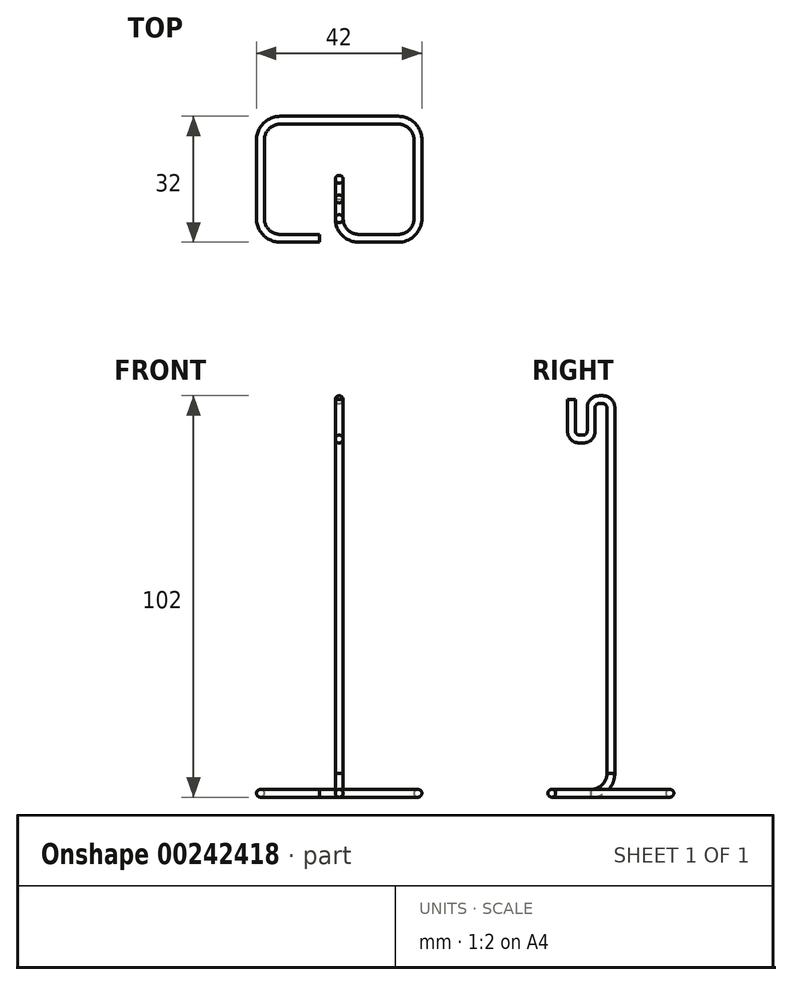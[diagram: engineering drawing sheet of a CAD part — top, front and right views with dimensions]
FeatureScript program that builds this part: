
annotation { "Feature Type Name" : "Feature", "Feature Type Description" : "" }
export const myFeature = defineFeature(function(context is Context, id is Id, definition is map)
    precondition{}
    {
        {
            var Q0;
            Q0=qCreatedBy(makeId("Top.planeOp"),FACE);
            var sketch = newSketch(context, id + "F0", { "sketchPlane" : qUnion([Q0])});
            skLineSegment(sketch, "E0.bottom", {"start": v(-15, 15) * mm, "end": v(15, 15) * mm});
            skLineSegment(sketch, "E0.top", {"start": v(-15, -15) * mm, "end": v(-5, -15) * mm});
            skLineSegment(sketch, "E0.left", {"start": v(-20, 10) * mm, "end": v(-20, -10) * mm});
            skLineSegment(sketch, "E0.right", {"start": v(20, 10) * mm, "end": v(20, -10) * mm});
            skLineSegment(sketch, "E1", {"start": v(0, 0) * mm, "end": v(0, -10) * mm});
            skLineSegment(sketch, "E2.trimOffspring", {"start": v(5, -15) * mm, "end": v(15, -15) * mm});
            skPoint(sketch, "E3.visualSharp", {"position": v(-20, -15) * mm});
            skArc(sketch, "E3.filletArc", {"start": v(-20, -10) * mm, "mid": v(-18.54, -13.54) * mm, "end": v(-15, -15) * mm});
            skPoint(sketch, "E4.visualSharp", {"position": v(-20, 15) * mm});
            skArc(sketch, "E4.filletArc", {"start": v(-15, 15) * mm, "mid": v(-18.54, 13.54) * mm, "end": v(-20, 10) * mm});
            skPoint(sketch, "E5.visualSharp", {"position": v(20, 15) * mm});
            skArc(sketch, "E5.filletArc", {"start": v(20, 10) * mm, "mid": v(18.54, 13.54) * mm, "end": v(15, 15) * mm});
            skPoint(sketch, "E6.visualSharp", {"position": v(20, -15) * mm});
            skArc(sketch, "E6.filletArc", {"start": v(15, -15) * mm, "mid": v(18.54, -13.54) * mm, "end": v(20, -10) * mm});
            skPoint(sketch, "E7.visualSharp", {"position": v(0, -15) * mm});
            skArc(sketch, "E7.filletArc", {"start": v(0, -10) * mm, "mid": v(1.46, -13.54) * mm, "end": v(5, -15) * mm});
            skSolve(sketch);
        }
        {
            var Q0;
            Q0=qCreatedBy(makeId("Right.planeOp"),FACE);
            var sketch = newSketch(context, id + "F1", { "sketchPlane" : qUnion([Q0])});
            skPoint(sketch, "E8.0", {"position": v(0, 0) * mm});
            skLineSegment(sketch, "E9", {"start": v(0, 0) * mm, "end": v(0, 98) * mm});
            skLineSegment(sketch, "E10", {"start": v(-2, 100) * mm, "end": v(-3, 100) * mm});
            skLineSegment(sketch, "E11", {"start": v(-5, 98) * mm, "end": v(-5, 92) * mm});
            skLineSegment(sketch, "E12", {"start": v(-7, 90) * mm, "end": v(-8, 90) * mm});
            skLineSegment(sketch, "E13", {"start": v(-10, 92) * mm, "end": v(-10, 100) * mm});
            skPoint(sketch, "E14.visualSharp", {"position": v(-10, 90) * mm});
            skArc(sketch, "E14.filletArc", {"start": v(-10, 92) * mm, "mid": v(-9.41, 90.59) * mm, "end": v(-8, 90) * mm});
            skPoint(sketch, "E15.visualSharp", {"position": v(-5, 90) * mm});
            skArc(sketch, "E15.filletArc", {"start": v(-7, 90) * mm, "mid": v(-5.59, 90.59) * mm, "end": v(-5, 92) * mm});
            skPoint(sketch, "E16.visualSharp", {"position": v(-5, 100) * mm});
            skArc(sketch, "E16.filletArc", {"start": v(-3, 100) * mm, "mid": v(-4.41, 99.41) * mm, "end": v(-5, 98) * mm});
            skPoint(sketch, "E17.visualSharp", {"position": v(0, 100) * mm});
            skArc(sketch, "E17.filletArc", {"start": v(0, 98) * mm, "mid": v(-0.59, 99.41) * mm, "end": v(-2, 100) * mm});
            skSolve(sketch);
        }
        {
            var Q0;
            Q0=sQuery(id+"F0.wireOp",VERTEX,"E0.top.end");
            var Q1;
            Q1=qCreatedBy(makeId("Right.planeOp"),FACE);
            cPlane(context, id + "F2", {"entities" : qUnion([Q0, Q1]), "cplaneType" : CPlaneType.PLANE_POINT, "offset" : 25 * mm, "width" : 150 * mm, "height" : 150 * mm});
        }
        {
            var Q0;
            Q0=qCreatedBy(id+"F2.planeOp",FACE);
            var sketch = newSketch(context, id + "F3", { "sketchPlane" : qUnion([Q0])});
            skPoint(sketch, "E18.0", {"position": v(-15, 0) * mm});
            skCircle(sketch, "E19", {"center": v(-15, 0) * mm, "radius": 1 * mm});
            skSolve(sketch);
        }
        {
            var Q0;
            Q0=makeQuery(id+"F3.imprint","IMPRINT",FACE,{"disambiguationData":[TD([[makeQuery(id+"F3.imprint","IMPRINT",EDGE,{"derivedFrom":sQuery(id+"F3.wireOp",EDGE,"E19")}),1.0]])]});
            var Q1;
            Q1=sQuery(id+"F0.wireOp",EDGE,"E0.top");
            var Q2;
            Q2=sQuery(id+"F0.wireOp",EDGE,"E3.filletArc");
            var Q3;
            Q3=sQuery(id+"F0.wireOp",EDGE,"E0.left");
            var Q4;
            Q4=sQuery(id+"F0.wireOp",EDGE,"E4.filletArc");
            var Q5;
            Q5=sQuery(id+"F0.wireOp",EDGE,"E0.bottom");
            var Q6;
            Q6=sQuery(id+"F0.wireOp",EDGE,"E5.filletArc");
            var Q7;
            Q7=sQuery(id+"F0.wireOp",EDGE,"E0.right");
            var Q8;
            Q8=sQuery(id+"F0.wireOp",EDGE,"E6.filletArc");
            var Q9;
            Q9=sQuery(id+"F0.wireOp",EDGE,"E2.trimOffspring");
            var Q10;
            Q10=sQuery(id+"F0.wireOp",EDGE,"E7.filletArc");
            var Q11;
            Q11=sQuery(id+"F0.wireOp",EDGE,"E1");
            var Q12;
            Q12=sQuery(id+"F1.wireOp",EDGE,"E9");
            var Q13;
            Q13=sQuery(id+"F1.wireOp",EDGE,"E17.filletArc");
            var Q14;
            Q14=sQuery(id+"F1.wireOp",EDGE,"E10");
            var Q15;
            Q15=sQuery(id+"F1.wireOp",EDGE,"E16.filletArc");
            var Q16;
            Q16=sQuery(id+"F1.wireOp",EDGE,"E11");
            var Q17;
            Q17=sQuery(id+"F1.wireOp",EDGE,"E15.filletArc");
            var Q18;
            Q18=sQuery(id+"F1.wireOp",EDGE,"E12");
            var Q19;
            Q19=sQuery(id+"F1.wireOp",EDGE,"E14.filletArc");
            var Q20;
            Q20=sQuery(id+"F1.wireOp",EDGE,"E13");
            sweep(context, id + "F4", {"profiles" : qUnion([Q0]), "path" : qUnion([Q1, Q2, Q3, Q4, Q5, Q6, Q7, Q8, Q9, Q10, Q11, Q12, Q13, Q14, Q15, Q16, Q17, Q18, Q19, Q20])});
        }
        {
            var Q0;
            Q0=qCreatedBy(makeId("Right.planeOp"),FACE);
            var sketch = newSketch(context, id + "F5", { "sketchPlane" : qUnion([Q0])});
            skLineSegment(sketch, "E20.0", {"start": v(0, 5) * mm, "end": v(0, 98) * mm, "construction": true});
            skLineSegment(sketch, "E21.0", {"start": v(-5, 0) * mm, "end": v(-10, 0) * mm, "construction": true});
            skPoint(sketch, "E22.visualSharp", {"position": v(0, 0) * mm});
            skArc(sketch, "E22.filletArc", {"start": v(-5, 0) * mm, "mid": v(-1.46, 1.46) * mm, "end": v(0, 5) * mm});
            skSolve(sketch);
        }
        {
            var Q0;
            Q0=qCreatedBy(makeId("Right.planeOp"),FACE);
            var sketch = newSketch(context, id + "F6", { "sketchPlane" : qUnion([Q0])});
            skPoint(sketch, "E23.0", {"position": v(-5, 0) * mm});
            skPoint(sketch, "E24.0", {"position": v(0, 5) * mm});
            skLineSegment(sketch, "E25.top", {"start": v(-5, 5) * mm, "end": v(0, 5) * mm});
            skLineSegment(sketch, "E25.left", {"start": v(-5, 0) * mm, "end": v(-5, 5) * mm});
            skLineSegment(sketch, "E26.bottom", {"start": v(-5, 5) * mm, "end": v(2.51, 5) * mm});
            skLineSegment(sketch, "E26.top", {"start": v(-5, -1.77) * mm, "end": v(2.51, -1.77) * mm});
            skLineSegment(sketch, "E26.left", {"start": v(-5, 5) * mm, "end": v(-5, -1.77) * mm});
            skLineSegment(sketch, "E26.right", {"start": v(2.51, 5) * mm, "end": v(2.51, -1.77) * mm});
            skSolve(sketch);
        }
        {
            var Q0;
            Q0 = qSketchRegion(id + "F6", true);
            extrude(context, id + "F7", {"entities" : qUnion([Q0]), "operationType" : NewBodyOperationType.REMOVE, "oppositeDirection" : true, "depth" : 3 * mm, "hasSecondDirection" : true, "secondDirectionOppositeDirection" : false, "secondDirectionDepth" : 3 * mm});
        }
        {
            var Q0;
            Q0=makeQuery(id+"F7.boolean.opBoolean","COPY",FACE,{"derivedFrom":makeQuery(id+"F7.opExtrude","SWEPT_FACE",FACE,{"disambiguationData":[OSD([sQuery(id+"F6.wireOp",EDGE,"E26.bottom")])]})});
            var Q1;
            Q1=sQuery(id+"F5.wireOp",EDGE,"E22.filletArc");
            sweep(context, id + "F8", {"profiles" : qUnion([Q0]), "path" : qUnion([Q1])});
        }
    });
